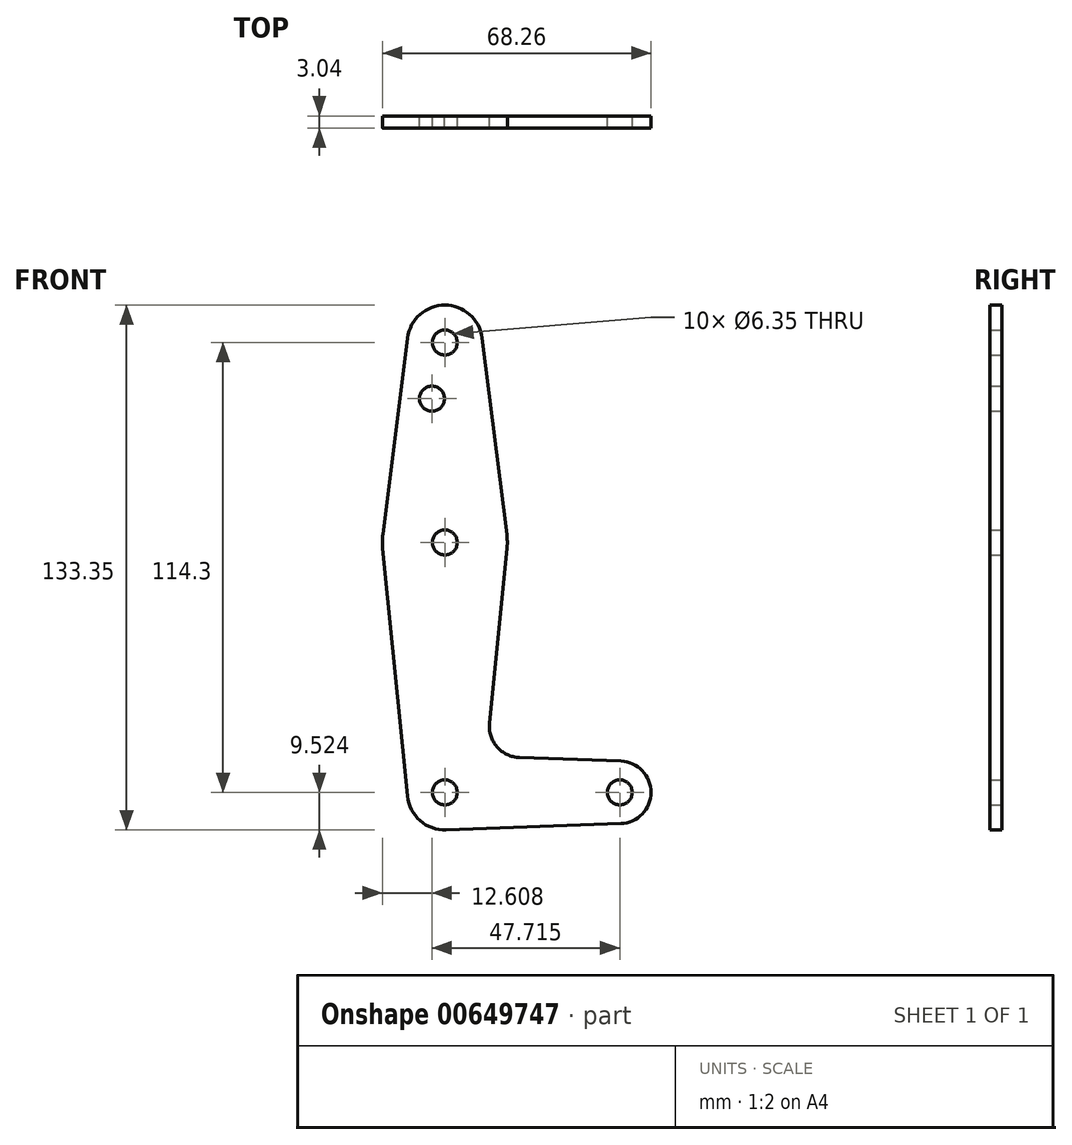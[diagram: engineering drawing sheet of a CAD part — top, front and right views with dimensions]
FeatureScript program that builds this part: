
annotation { "Feature Type Name" : "Feature", "Feature Type Description" : "" }
export const myFeature = defineFeature(function(context is Context, id is Id, definition is map)
    precondition{}
    {
        {
            var Q0;
            Q0=qCreatedBy(makeId("Front.planeOp"),FACE);
            var sketch = newSketch(context, id + "F0", { "sketchPlane" : qUnion([Q0])});
            skLineSegment(sketch, "E0", {"start": v(-26.47, 56.1) * mm, "end": v(-26.47, -58.2) * mm, "construction": true});
            skLineSegment(sketch, "E1", {"start": v(-26.47, -58.2) * mm, "end": v(17.98, -58.2) * mm, "construction": true});
            skCircle(sketch, "E2", {"center": v(-26.47, 56.1) * mm, "radius": 9.53 * mm});
            skCircle(sketch, "E3", {"center": v(-26.47, -58.2) * mm, "radius": 9.53 * mm});
            skCircle(sketch, "E4", {"center": v(17.98, -58.2) * mm, "radius": 7.94 * mm});
            skCircle(sketch, "E5", {"center": v(-26.47, 5.3) * mm, "radius": 15.88 * mm});
            skLineSegment(sketch, "E6", {"start": v(-35.92, 57.28) * mm, "end": v(-42.22, 7.28) * mm});
            skLineSegment(sketch, "E7", {"start": v(-15.13, -40.61) * mm, "end": v(-10.67, 3.7) * mm});
            skLineSegment(sketch, "E8", {"start": v(-42.26, 3.7) * mm, "end": v(-35.95, -59.16) * mm});
            skLineSegment(sketch, "E9", {"start": v(-17.02, 57.28) * mm, "end": v(-10.72, 7.28) * mm});
            skLineSegment(sketch, "E10", {"start": v(-7.5, -49.35) * mm, "end": v(18.27, -50.27) * mm});
            skLineSegment(sketch, "E11", {"start": v(-26.13, -67.73) * mm, "end": v(18.27, -66.14) * mm});
            skCircle(sketch, "E12", {"center": v(-26.47, 56.1) * mm, "radius": 3.18 * mm});
            skCircle(sketch, "E13", {"center": v(-26.47, 5.3) * mm, "radius": 3.18 * mm});
            skCircle(sketch, "E14", {"center": v(-26.47, -58.2) * mm, "radius": 3.18 * mm});
            skCircle(sketch, "E15", {"center": v(17.98, -58.2) * mm, "radius": 3.18 * mm});
            skCircle(sketch, "E16", {"center": v(-29.73, 41.82) * mm, "radius": 3.18 * mm});
            skArc(sketch, "E17.filletArc", {"start": v(-15.13, -40.61) * mm, "mid": v(-13.2, -46.64) * mm, "end": v(-7.5, -49.35) * mm});
            skSolve(sketch);
        }
        {
            var Q0;
            Q0=makeQuery(id+"F0.imprint","IMPRINT",FACE,{"disambiguationData":[TD([[makeQuery(id+"F0.imprint","IMPRINT",EDGE,{"derivedFrom":sQuery(id+"F0.wireOp",EDGE,"E12")}),-1.0]])]});
            var Q1;
            {var subQ1=sQuery(id+"F0.wireOp",EDGE,"E6");Q1=makeQuery(id+"F0.imprint","IMPRINT",FACE,{"disambiguationData":[TD([[makeQuery(id+"F0.imprint","IMPRINT",EDGE,{"derivedFrom":subQ1}),1.0]])]});}
            var Q2;
            Q2=makeQuery(id+"F0.imprint","IMPRINT",FACE,{"disambiguationData":[TD([[makeQuery(id+"F0.imprint","IMPRINT",EDGE,{"derivedFrom":sQuery(id+"F0.wireOp",EDGE,"E13")}),-1.0]])]});
            var Q3;
            {var subQ0=sQuery(id+"F0.wireOp",EDGE,"E7");Q3=makeQuery(id+"F0.imprint","IMPRINT",FACE,{"disambiguationData":[TD([[makeQuery(id+"F0.imprint","IMPRINT",EDGE,{"derivedFrom":subQ0}),1.0]])]});}
            var Q4;
            Q4=makeQuery(id+"F0.imprint","IMPRINT",FACE,{"disambiguationData":[TD([[makeQuery(id+"F0.imprint","IMPRINT",EDGE,{"derivedFrom":sQuery(id+"F0.wireOp",EDGE,"E14")}),-1.0]])]});
            var Q5;
            Q5=makeQuery(id+"F0.imprint","IMPRINT",FACE,{"disambiguationData":[TD([[makeQuery(id+"F0.imprint","IMPRINT",EDGE,{"derivedFrom":sQuery(id+"F0.wireOp",EDGE,"E15")}),-1.0]])]});
            extrude(context, id + "F1", {"entities" : qUnion([Q0, Q1, Q2, Q3, Q4, Q5]), "endBound" : BoundingType.SYMMETRIC, "depth" : 3.05 * mm, "offsetDistance" : 25.4 * mm});
        }
    });
